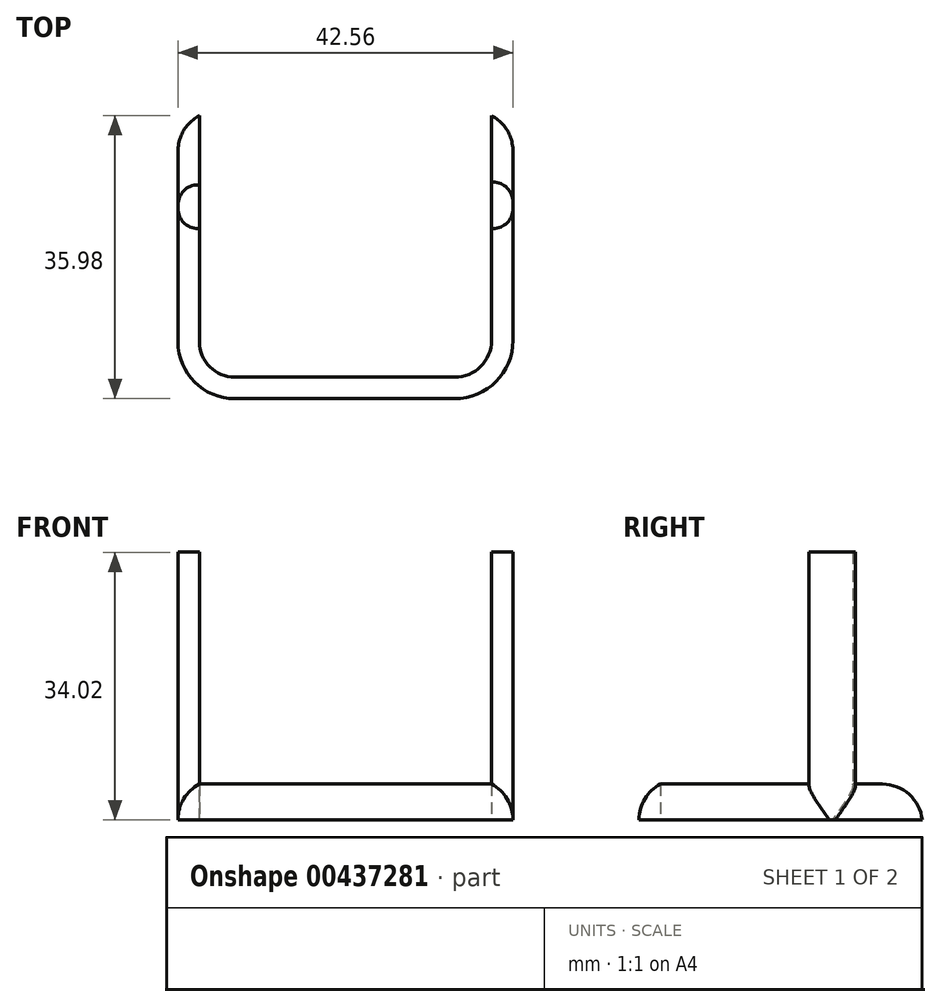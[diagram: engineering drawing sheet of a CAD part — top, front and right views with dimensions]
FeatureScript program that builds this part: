
annotation { "Feature Type Name" : "Feature", "Feature Type Description" : "" }
export const myFeature = defineFeature(function(context is Context, id is Id, definition is map)
    precondition{}
    {
        {
            var Q0;
            Q0=qCreatedBy(makeId("Top.planeOp"),FACE);
            var sketch = newSketch(context, id + "F0", { "sketchPlane" : qUnion([Q0])});
            skLineSegment(sketch, "E0", {"start": v(-37.34, 0) * mm, "end": v(-37.34, -28.76) * mm});
            skLineSegment(sketch, "E1", {"start": v(-32.73, -33.37) * mm, "end": v(-4.79, -33.37) * mm});
            skLineSegment(sketch, "E2", {"start": v(0, -28.58) * mm, "end": v(0, 0) * mm});
            skPoint(sketch, "E3.visualSharp", {"position": v(-37.34, -33.37) * mm});
            skArc(sketch, "E3.filletArc", {"start": v(-37.34, -28.76) * mm, "mid": v(-36, -32.02) * mm, "end": v(-32.73, -33.37) * mm});
            skPoint(sketch, "E4.visualSharp", {"position": v(0, -33.37) * mm});
            skArc(sketch, "E4.filletArc", {"start": v(-4.79, -33.37) * mm, "mid": v(-1.4, -31.97) * mm, "end": v(0, -28.58) * mm});
            skSolve(sketch);
        }
        {
            var Q0;
            Q0=qCreatedBy(makeId("Front.planeOp"),FACE);
            var sketch = newSketch(context, id + "F1", { "sketchPlane" : qUnion([Q0])});
            skLineSegment(sketch, "E5.bottom", {"start": v(-37.22, 0) * mm, "end": v(-39.95, 0) * mm});
            skLineSegment(sketch, "E5.top", {"start": v(-37.22, -4.56) * mm, "end": v(-39.95, -4.56) * mm});
            skLineSegment(sketch, "E5.left", {"start": v(-37.22, 0) * mm, "end": v(-37.22, -4.56) * mm});
            skLineSegment(sketch, "E5.right", {"start": v(-39.95, 0) * mm, "end": v(-39.95, -4.56) * mm});
            skSolve(sketch);
        }
        {
            var Q0;
            Q0=makeQuery(id+"F1.imprint","IMPRINT",FACE,{"disambiguationData":[TD([[makeQuery(id+"F1.imprint","IMPRINT",EDGE,{"derivedFrom":sQuery(id+"F1.wireOp",EDGE,"E5.bottom")}),1.0]])]});
            var Q1;
            Q1=sQuery(id+"F0.wireOp",EDGE,"E0");
            var Q2;
            Q2=sQuery(id+"F0.wireOp",EDGE,"E3.filletArc");
            var Q3;
            Q3=sQuery(id+"F0.wireOp",EDGE,"E1");
            var Q4;
            Q4=sQuery(id+"F0.wireOp",EDGE,"E4.filletArc");
            var Q5;
            Q5=sQuery(id+"F0.wireOp",EDGE,"E2");
            sweep(context, id + "F2", {"profiles" : qUnion([Q0]), "path" : qUnion([Q1, Q2, Q3, Q4, Q5])});
        }
        {
            var Q0;
            Q0=makeQuery(id+"F2.opSweep","SWEPT_FACE",FACE,{"disambiguationData":[OSD([sQuery(id+"F0.wireOp",EDGE,"E0"),sQuery(id+"F1.wireOp",EDGE,"E5.bottom")])]});
            var sketch = newSketch(context, id + "F3", { "sketchPlane" : qUnion([Q0])});
            skLineSegment(sketch, "E6.bottom", {"start": v(-39.95, -8.82) * mm, "end": v(-37.22, -8.82) * mm});
            skLineSegment(sketch, "E6.top", {"start": v(-39.95, -14.38) * mm, "end": v(-37.22, -14.38) * mm});
            skLineSegment(sketch, "E6.left", {"start": v(-39.95, -8.82) * mm, "end": v(-39.95, -14.38) * mm});
            skLineSegment(sketch, "E6.right", {"start": v(-37.22, -8.82) * mm, "end": v(-37.22, -14.38) * mm});
            skPoint(sketch, "E7.firstSnap0", {"position": v(-0.13, -14.3) * mm});
            skLineSegment(sketch, "E7.bottom", {"start": v(-0.13, -14.38) * mm, "end": v(2.61, -14.38) * mm});
            skLineSegment(sketch, "E7.top", {"start": v(-0.13, -8.47) * mm, "end": v(2.61, -8.47) * mm});
            skLineSegment(sketch, "E7.left", {"start": v(-0.13, -14.38) * mm, "end": v(-0.13, -8.47) * mm});
            skLineSegment(sketch, "E7.right", {"start": v(2.61, -14.38) * mm, "end": v(2.61, -8.47) * mm});
            skSolve(sketch);
        }
        {
            var Q0;
            Q0=qSketchRegion(id+"F3",true);
            extrude(context, id + "F4", {"entities" : qUnion([Q0]), "operationType" : NewBodyOperationType.ADD, "depth" : 29.46 * mm});
        }
        {
            var Q0;
            Q0=makeQuery(id+"F4.opExtrude","SWEPT_EDGE",EDGE,{"disambiguationData":[OSD([sQuery(id+"F0.wireOp",EDGE,"E0"),sQuery(id+"F1.wireOp",EDGE,"E5.bottom"),sQuery(id+"F1.wireOp",EDGE,"E5.right"),sQuery(id+"F3.wireOp",EDGE,"E6.top"),sQuery(id+"F3.wireOp",EDGE,"E6.left")])]});
            fillet(context, id + "F5", {"entities" : qUnion([Q0]), "radius" : 2.54 * mm, "tangentPropagation" : true, "allowEdgeOverflow" : false});
        }
        {
            var Q0;
            Q0=makeQuery(id+"F4.opExtrude","SWEPT_EDGE",EDGE,{"disambiguationData":[OSD([sQuery(id+"F0.wireOp",EDGE,"E2"),sQuery(id+"F1.wireOp",EDGE,"E5.bottom"),sQuery(id+"F1.wireOp",EDGE,"E5.right"),sQuery(id+"F3.wireOp",EDGE,"E7.bottom"),sQuery(id+"F3.wireOp",EDGE,"E7.right")])]});
            fillet(context, id + "F6", {"entities" : qUnion([Q0]), "radius" : 2.54 * mm, "tangentPropagation" : true, "allowEdgeOverflow" : false});
        }
        {
            var Q0;
            Q0=makeQuery(id+"F4.opExtrude","SWEPT_EDGE",EDGE,{"disambiguationData":[OSD([sQuery(id+"F0.wireOp",EDGE,"E2"),sQuery(id+"F1.wireOp",EDGE,"E5.bottom"),sQuery(id+"F1.wireOp",EDGE,"E5.right"),sQuery(id+"F3.wireOp",EDGE,"E7.top"),sQuery(id+"F3.wireOp",EDGE,"E7.right")])]});
            fillet(context, id + "F7", {"entities" : qUnion([Q0]), "radius" : 2.54 * mm, "tangentPropagation" : true, "allowEdgeOverflow" : false});
        }
        {
            var Q0;
            Q0=makeQuery(id+"F4.opExtrude","SWEPT_EDGE",EDGE,{"disambiguationData":[OSD([sQuery(id+"F0.wireOp",EDGE,"E0"),sQuery(id+"F1.wireOp",EDGE,"E5.bottom"),sQuery(id+"F1.wireOp",EDGE,"E5.right"),sQuery(id+"F3.wireOp",EDGE,"E6.bottom"),sQuery(id+"F3.wireOp",EDGE,"E6.left")])]});
            fillet(context, id + "F8", {"entities" : qUnion([Q0]), "radius" : 2.54 * mm, "tangentPropagation" : true, "allowEdgeOverflow" : false});
        }
        {
            var Q0;
            Q0=makeQuery(id+"F2.opSweep","CAP_EDGE",EDGE,{"disambiguationData":[OSD([sQuery(id+"F0.wireOp",VERTEX,"E0.start"),sQuery(id+"F1.wireOp",EDGE,"E5.bottom")])],"isStart":true});
            fillet(context, id + "F9", {"entities" : qUnion([Q0]), "radius" : 5.08 * mm, "tangentPropagation" : true, "allowEdgeOverflow" : false});
        }
        {
            var Q0;
            Q0=makeQuery(id+"F2.opSweep","CAP_EDGE",EDGE,{"disambiguationData":[OSD([sQuery(id+"F0.wireOp",VERTEX,"E2.end"),sQuery(id+"F1.wireOp",EDGE,"E5.bottom")])],"isStart":false});
            fillet(context, id + "F10", {"entities" : qUnion([Q0]), "radius" : 5.08 * mm, "tangentPropagation" : true, "allowEdgeOverflow" : false});
        }
        {
            var Q0;
            {var subQ0=sQuery(id+"F1.wireOp",EDGE,"E5.right");var subQ1=sQuery(id+"F0.wireOp",EDGE,"E2");var subQ2=sQuery(id+"F1.wireOp",EDGE,"E5.bottom");Q0=makeQuery(id+"F4.boolean.opBoolean","SPLIT",EDGE,{"disambiguationData":[TD([makeQuery(id+"F4.opExtrude","SWEPT_FACE",FACE,{"disambiguationData":[OSD([sQuery(id+"F3.wireOp",EDGE,"E7.top")])]})])],"derivedFrom":makeQuery(id+"F2.opSweep","SWEPT_EDGE",EDGE,{"disambiguationData":[OSD([subQ1,subQ2,subQ0])]})});}
            fillet(context, id + "F11", {"entities" : qUnion([Q0]), "radius" : 5.08 * mm, "tangentPropagation" : true, "allowEdgeOverflow" : false});
        }
        {
            var Q0;
            {var subQ0=sQuery(id+"F1.wireOp",EDGE,"E5.right");var subQ1=sQuery(id+"F1.wireOp",EDGE,"E5.bottom");var subQ2=sQuery(id+"F0.wireOp",EDGE,"E2");Q0=makeQuery(id+"F4.boolean.opBoolean","SPLIT",EDGE,{"disambiguationData":[TD([makeQuery(id+"F4.opExtrude","SWEPT_FACE",FACE,{"disambiguationData":[OSD([sQuery(id+"F3.wireOp",EDGE,"E7.bottom")])]})])],"derivedFrom":makeQuery(id+"F2.opSweep","SWEPT_EDGE",EDGE,{"disambiguationData":[OSD([subQ2,subQ1,subQ0])]})});}
            fillet(context, id + "F12", {"entities" : qUnion([Q0]), "radius" : 5.08 * mm, "tangentPropagation" : true, "allowEdgeOverflow" : false});
        }
        {
            var Q0;
            {var subQ0=sQuery(id+"F1.wireOp",EDGE,"E5.bottom");var subQ1=sQuery(id+"F0.wireOp",EDGE,"E0");var subQ2=sQuery(id+"F1.wireOp",EDGE,"E5.right");Q0=makeQuery(id+"F4.boolean.opBoolean","SPLIT",EDGE,{"disambiguationData":[TD([makeQuery(id+"F4.opExtrude","SWEPT_FACE",FACE,{"disambiguationData":[OSD([sQuery(id+"F3.wireOp",EDGE,"E6.bottom")])]})])],"derivedFrom":makeQuery(id+"F2.opSweep","SWEPT_EDGE",EDGE,{"disambiguationData":[OSD([subQ1,subQ0,subQ2])]})});}
            fillet(context, id + "F13", {"entities" : qUnion([Q0]), "radius" : 5.08 * mm, "tangentPropagation" : true, "allowEdgeOverflow" : false});
        }
    });
